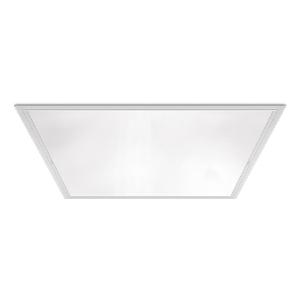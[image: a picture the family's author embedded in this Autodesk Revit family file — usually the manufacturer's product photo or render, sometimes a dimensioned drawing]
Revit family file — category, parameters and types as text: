
# Revit family: 3f_filippi_-_l_340_luce_diffusa_lgs_ip65v_3f_filippi_-_23974_-_l_340_45w-840_lgs_ip65v_596x596
name_source: partatom
category: Lighting Fixtures
units: mm (PartAtom-declared; Revit-internal decimal feet)

## family parameters
Cut with Voids When Loaded = No
Host = Face
Light Source = No
Part Type = Normal
Room Calculation Point = No
Round Connector Dimension = Use Diameter
Shared = No

## types (1)
- 3F Filippi - L 340 Luce Diffusa LGS IP65V (1 x LED, 6537 lm, 52 W, 4000 K)
    Apparent Load = 52 VA
    Approval mark = ENEC
    CIE Flux Codes = 67 92 98 100 100
    Color Rendering = 80
    Color Temperature = 4000 K
    Control Gear = Electronic ballast
    Default Elevation = 1800 mm
    Description = ILLUMINOTECHNICAL
Luminous efficiency 100% (DLOR 100%, ULOR 0%).
Initial luminous flux of the luminaire 6537 lm.
Direct symmetric distribution.
Installation Interdistance Transv.D = 1.19 x hu - Long.D = 1.17 x hu.
Average luminance <3000 cd/m² for radial angles >65°.
Tabular UGR (CIE 117 - 4H-8H; S=0.25H; 70/50/20): RUG 18.3 - 18.3.
Beam angle: 87° - 86°.
Luminous efficacy 126 lm/W.
Lifetime (L93/B10): 30000 h. (tq+25°C)
Lifetime (L90/B10): 50000 h. (tq+25°C)
Lifetime (L85/B10): 80000 h. (tq+25°C)
Lifetime (L80/B10): 100000 h. (tq+25°C)
Sudden decreased luminous flux after 50000 hours: 0% (C0).
Photobiological safety in compliance with IEC/TR 62778: RG0 risk exempt, (IEC 62471).
In compliance with IEC/EN 62722-2-1 - IEC/EN 62717 standards.

SOURCE
Squared LED module 45W/840.
Energy efficiency class (UE 2019/2020 - UE 2019/2015): C.
CIE 13.3 Colour rendering index: CRI >80 (R9 <50%).
IES TM-30 Fidelity Index: Rf = 84 Rg = 95.
CCT nominal colour temperature 4000 K.
Colour initial tolerance (MacAdam): SDCM 3.

MECHANICAL
Housing in hot-galvanised steel, painted in white polyester.
Perimetral frame in white polycarbonate.
LGS micro-prismatic flat diffuser in transparent methacrylate (PMMA), multi-lenticular exterior, anti-glare.
Anti-glare opal polycarbonate filter for brightness uniformity.
Luminaire with limited surface temperature. - D - (EN 60598-2-24)
Dimensions: 596x596 mm, height 80 mm. Weight 4.45 kg.
IP65 protection degree for exposed part, IP40 for recessed part.
Mechanical strength to impacts IK06 (1 joule).
Glow-wire test resistance 650°C.

ELECTRICAL
Wiring on a separate unit.
Halogen Free electronic wiring 230V-50/60Hz, power factor 0.95, THD <25%, constant output current, SELV, class II, 1 driver.
Power of the luminaire 52 W.
CE - IEC 60598-1 - EN 60598-1.
SAFE FLICKER: PstLM=<1 and SVM=<0.4 (IEC TR 61547-1 and IEC TR 63158), to ensure a more comfortable and safe light.
Luminaire compliant with EN 60598-2-22 for power supply from a centralised emergency system CPSS (Central Power Supply System), not incorporated in the luminaire - high risk areas excluded. The default power and flux are 100% in AC and 100% in DC.
Ambient temperature from 0°C to +40°C.
Temperature class T6 max 85°C.
Relative humidity UR: <85%.

INSTALLATION
Lay-on or pull-up recessed fitting using frame accessory.
All accessories dedicated to this product are available on the Catalog and on our website www.3F-Filippi.com.

APPLICATIONS
Suitable product for food production plants (HACCP), IFS (Food Version 6), BRC (GSFS Food Version 7).
In environments requiring protection and simplified cleaning.
Hospitals, pharmaceutical, chemical, aseptic laboratories, sterilised rooms.
Environments: with VDTs, meeting rooms, offices.
Environments: architectural, commercial, staterooms, banks.
Environments where demanding visual tasks are performed and soft diffuse light is required for optimal visual comfort and total shielding of the light source.

WARNING
Luminaire designed for disposal/recycling at end-of-life.
Replaceable (LED only) light source by a professional. Replaceable control gear by a professional.
    Height = 0 mm  [stored 0 ft]
    Lamp = 1 x LED
    Lamp Light Flux = 6537 lm
    Lamp Power = 52 W
    Lamp count = 1
    Length = 596 mm
    Lifetime = 50000 h
    Luminous efficacy = 126 lm/W
    Manufacturer = 3F Filippi
    ModVariant = No
    Model = 3F Filippi - 23974 - L 340 45W-840 LGS IP65V 596x596
    Mounting Place = Ceiling
    Mounting Type = Recessed
    Number of Poles = 1
    OnlyDefault = Yes
    Power Factor = 1
    Product Name = 3F Filippi - L 340 Luce Diffusa LGS IP65V
    Product group = recessed luminaire
    ProductGroupID = 4
    Protection Class = Protection class II
    Protection Degree = IP 40
    RLX_Detail_Level = 1
    RLX_Emergency_Light_Flux = 0 lm
    RLX_Emergency_Type = 0
    RLX_Emergency_Type_DB = No
    RlxData = <blob elided: 154689 chars, md5=c14b6502>
    Socket = socket
    Standby Power = 0 W
    System Light Flux = 6537 lm
    System Power = 52 W
    Type Comments = Product without accessories
    Type Image = 3ffilippi_l_340_luce_diffusa_lgs_ip65v.jpg
    URL = http://relux.com
    VarID = ---
    Voltage = 0 V
    Weight = 0.00 kg
    Width = 596 mm

note: [stored X ft] marks values corroborated as IEEE doubles in the binary element streams (Revit-internal decimal feet)

## geometry (parser evidence)
native form markers: Blend x4, Sweep x11
no freeform markers — native parametric forms only
